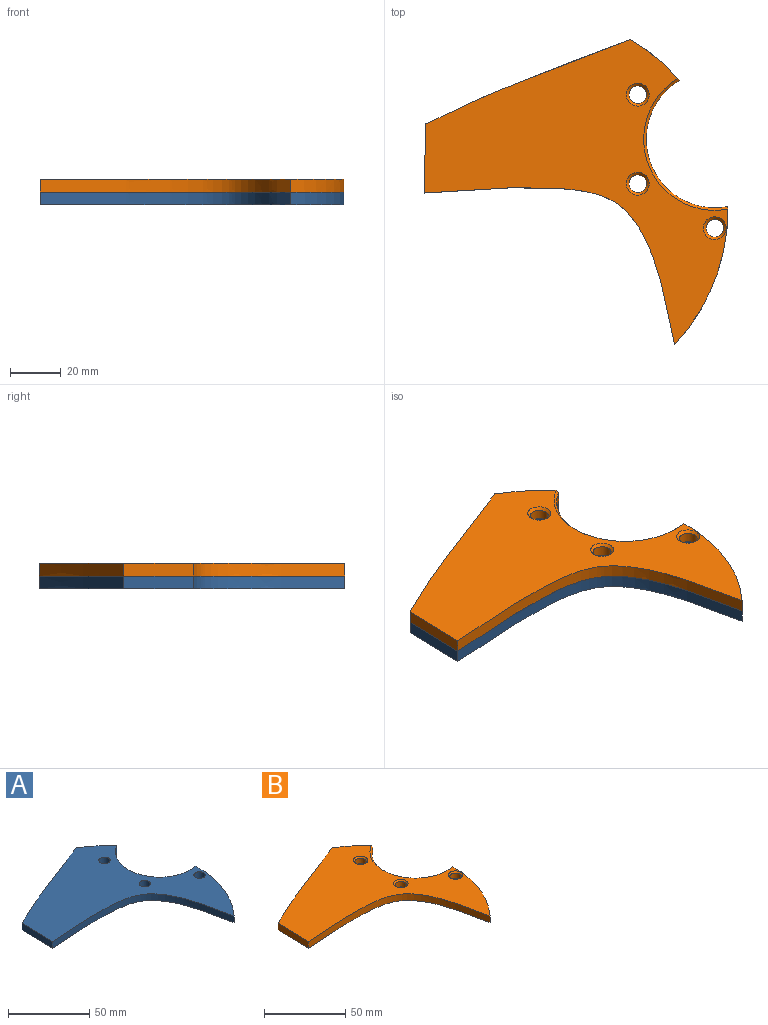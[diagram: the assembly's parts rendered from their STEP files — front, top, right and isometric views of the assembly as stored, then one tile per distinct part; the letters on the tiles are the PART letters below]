
ASSEMBLY  parts=2 mates=1
PART A: 11 faces, bbox 119.4x121.8x5 mm
  f0: plane 121.78x119.45mm, normal (0,0,1), area 5329.8mm2, adj f1,f2,f3,f5,f6,f7,f8,f9
  f1: cylinder r=3.5mm len=7mm, axis (0,0,-1), area 110mm2, adj f0,f4
  f2: cylinder r=3.5mm len=7mm, axis (0,0,-1), area 110mm2, adj f0,f4
  f3: cylinder r=3.5mm len=7mm, axis (0,0,-1), area 110mm2, adj f0,f4
  f4: plane 121.78x119.45mm, normal (0,0,-1), area 5329.8mm2, adj f1,f2,f3,f5,f6,f7,f8,f9
  f5: cylinder r=77.62mm len=54.24mm, axis (0,0,-1), area 298mm2, adj f0,f4,f6,f10
  f6: extruded ~98.51x61.73mm, area 691mm2, adj f0,f4,f5,f7
  f7: plane 27.14x5mm, normal (-1,0.02,0), area 135.7mm2, adj f0,f4,f6,f8
  f8: extruded ~80.43x33.26mm, area 435.4mm2, adj f0,f4,f7,f9
  f9: cylinder r=77.62mm len=19.37mm, axis (0,0,-1), area 126.5mm2, adj f0,f4,f8,f10
  f10: cylinder r=27mm len=50.16mm, axis (0,0,-1), area 376.9mm2, adj f0,f4,f5,f9
PART B: 15 faces, bbox 119.6x121.8x5 mm
  f0: cylinder r=27mm len=50.16mm, axis (0,0,-1), area 301.5mm2, adj f1,f8,f10,f14
  f1: cylinder r=77.62mm len=19.37mm, axis (0,0,-1), area 126mm2, adj f0,f2,f9,f10,f14
  f2: extruded ~80.43x33.26mm, area 435.4mm2, adj f1,f3,f9,f14
  f3: plane 27.14x5mm, normal (-1,0.02,0), area 135.7mm2, adj f2,f4,f9,f14
  f4: extruded ~98.51x61.73mm, area 691mm2, adj f3,f8,f9,f14
  f5: cylinder r=3.5mm len=7mm, axis (0,0,-1), area 88mm2, adj f13,f14
  f6: cylinder r=3.5mm len=7mm, axis (0,0,-1), area 88mm2, adj f11,f14
  f7: cylinder r=3.5mm len=7mm, axis (0,0,-1), area 88mm2, adj f12,f14
  f8: cylinder r=77.62mm len=54.24mm, axis (0,0,-1), area 297.5mm2, adj f0,f4,f9,f10,f14
  f9: plane 121.78x119.45mm, normal (0,0,1), area 5177.8mm2, adj f1,f2,f3,f4,f8,f10,f11,f12
  f10: cone r=27mm half-angle=45deg, axis (0,0,1), area 108.3mm2, adj f0,f1,f8,f9
  f11: cone r=3.5mm half-angle=45deg, axis (0,0,1), area 35.5mm2, adj f6,f9
  f12: cone r=3.5mm half-angle=45deg, axis (0,0,1), area 35.5mm2, adj f7,f9
  f13: cone r=3.5mm half-angle=45deg, axis (0,0,1), area 35.5mm2, adj f5,f9
  f14: plane 121.78x119.45mm, normal (0,0,-1), area 5329.8mm2, adj f0,f1,f2,f3,f4,f5,f6,f7
PLACE A t=(127.92,92.9,-137.81)mm
PLACE B t=(127.92,92.9,-137.81)mm
MATE fastened A.f10 <-> B.f0  axis (0,0,1) through (127.92,92.9,-137.81)mm
